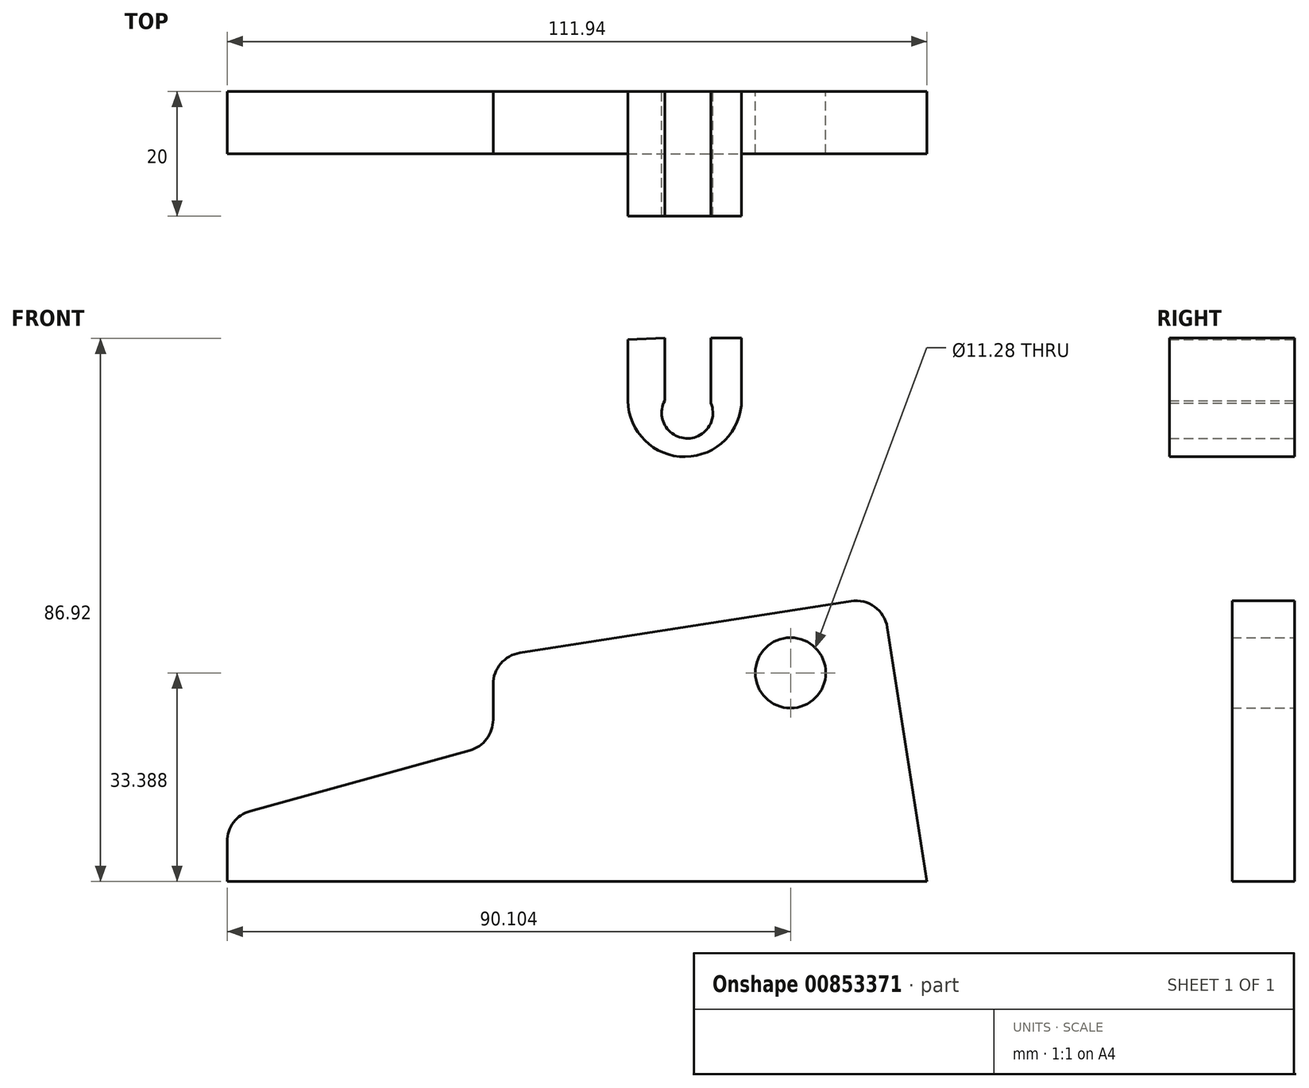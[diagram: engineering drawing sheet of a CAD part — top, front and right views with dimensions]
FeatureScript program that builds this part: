
annotation { "Feature Type Name" : "Feature", "Feature Type Description" : "" }
export const myFeature = defineFeature(function(context is Context, id is Id, definition is map)
    precondition{}
    {
        {
            var Q0;
            Q0=qCreatedBy(makeId("Front.planeOp"),FACE);
            var sketch = newSketch(context, id + "F0", { "sketchPlane" : qUnion([Q0])});
            skLineSegment(sketch, "E0", {"start": v(49.48, -22.03) * mm, "end": v(-42.54, -22.03) * mm});
            skLineSegment(sketch, "E1", {"start": v(-42.54, -22.03) * mm, "end": v(-42.54, -11.77) * mm});
            skLineSegment(sketch, "E2", {"start": v(-42.54, -11.77) * mm, "end": v(0, 0) * mm});
            skLineSegment(sketch, "E3", {"start": v(0, 0) * mm, "end": v(0, 13.88) * mm});
            skLineSegment(sketch, "E4", {"start": v(0, 13.88) * mm, "end": v(62.25, 23.62) * mm});
            skLineSegment(sketch, "E5", {"start": v(69.4, -22.03) * mm, "end": v(38.02, -22.03) * mm});
            skLineSegment(sketch, "E6", {"start": v(69.4, -22.03) * mm, "end": v(62.25, 23.62) * mm});
            skSolve(sketch);
        }
        {
            var Q0;
            Q0 = qSketchRegion(id + "F0", true);
            extrude(context, id + "F1", {"entities" : qUnion([Q0]), "depth" : 10 * mm, "offsetDistance" : 25.4 * mm});
        }
        {
            var Q0;
            Q0=makeQuery(id+"F1.opExtrude","SWEPT_EDGE",EDGE,{"disambiguationData":[OSD([sQuery(id+"F0.wireOp",EDGE,"E4"),sQuery(id+"F0.wireOp",EDGE,"E6")])]});
            var Q1;
            Q1=makeQuery(id+"F1.opExtrude","SWEPT_EDGE",EDGE,{"disambiguationData":[OSD([sQuery(id+"F0.wireOp",EDGE,"E3"),sQuery(id+"F0.wireOp",EDGE,"E4")])]});
            var Q2;
            Q2=makeQuery(id+"F1.opExtrude","SWEPT_EDGE",EDGE,{"disambiguationData":[OSD([sQuery(id+"F0.wireOp",EDGE,"E2"),sQuery(id+"F0.wireOp",EDGE,"E3")])]});
            var Q3;
            Q3=makeQuery(id+"F1.opExtrude","SWEPT_EDGE",EDGE,{"disambiguationData":[OSD([sQuery(id+"F0.wireOp",EDGE,"E1"),sQuery(id+"F0.wireOp",EDGE,"E2")])]});
            fillet(context, id + "F2", {"entities" : qUnion([Q0, Q1, Q2, Q3]), "radius" : 5.08 * mm, "tangentPropagation" : true, "allowEdgeOverflow" : false});
        }
        {
            var Q0;
            Q0=qCreatedBy(makeId("Front.planeOp"),FACE);
            var sketch = newSketch(context, id + "F3", { "sketchPlane" : qUnion([Q0])});
            skCircle(sketch, "E7", {"center": v(47.56, 11.36) * mm, "radius": 5.64 * mm});
            skSolve(sketch);
        }
        {
            var Q0;
            Q0 = qSketchRegion(id + "F3", true);
            extrude(context, id + "F4", {"entities" : qUnion([Q0]), "operationType" : NewBodyOperationType.REMOVE, "depth" : 93.35 * mm, "offsetDistance" : 25.4 * mm});
        }
        {
            var Q0;
            Q0=qCreatedBy(makeId("Front.planeOp"),FACE);
            var sketch = newSketch(context, id + "F5", { "sketchPlane" : qUnion([Q0])});
            skArc(sketch, "E8", {"start": v(27.45, 54.9) * mm, "mid": v(30.83, 48.86) * mm, "end": v(34.85, 54.5) * mm});
            skLineSegment(sketch, "E9", {"start": v(27.45, 54.9) * mm, "end": v(27.45, 64.9) * mm});
            skLineSegment(sketch, "E10", {"start": v(34.85, 54.5) * mm, "end": v(34.85, 64.9) * mm});
            skLineSegment(sketch, "E11", {"start": v(39.74, 64.9) * mm, "end": v(39.74, 55.02) * mm});
            skLineSegment(sketch, "E12", {"start": v(21.54, 64.65) * mm, "end": v(21.54, 54.9) * mm});
            skLineSegment(sketch, "E13", {"start": v(21.54, 54.9) * mm, "end": v(21.54, 64.65) * mm});
            skArc(sketch, "E14", {"start": v(21.54, 54.9) * mm, "mid": v(30.7, 45.93) * mm, "end": v(39.74, 55.02) * mm});
            skLineSegment(sketch, "E15", {"start": v(34.85, 64.9) * mm, "end": v(39.74, 64.9) * mm});
            skLineSegment(sketch, "E16", {"start": v(27.45, 64.9) * mm, "end": v(21.54, 64.65) * mm});
            skSolve(sketch);
        }
        {
            var Q0;
            Q0 = qSketchRegion(id + "F5", true);
            extrude(context, id + "F6", {"entities" : qUnion([Q0]), "depth" : 20 * mm, "offsetDistance" : 25.4 * mm});
        }
    });
